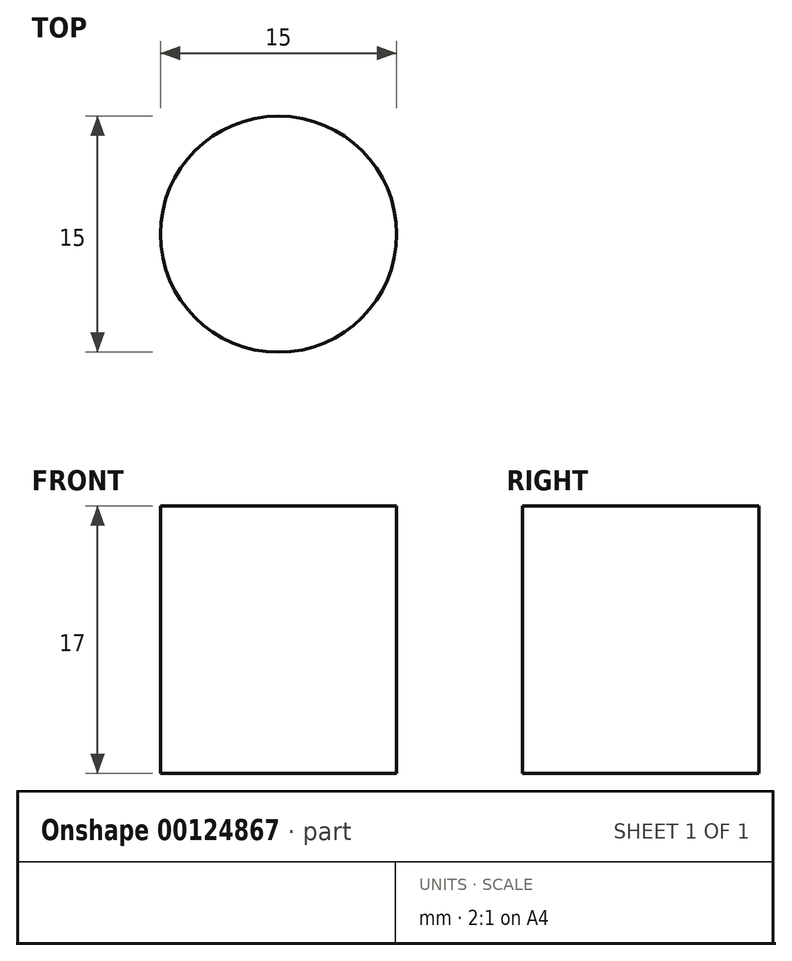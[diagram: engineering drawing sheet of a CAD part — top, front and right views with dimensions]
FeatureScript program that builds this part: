
annotation { "Feature Type Name" : "Feature", "Feature Type Description" : "" }
export const myFeature = defineFeature(function(context is Context, id is Id, definition is map)
    precondition{}
    {
        {
            var Q0;
            Q0=qCreatedBy(makeId("Top.planeOp"),FACE);
            var sketch = newSketch(context, id + "F0", { "sketchPlane" : qUnion([Q0])});
            skCircle(sketch, "E0", {"center": v(0, 0) * mm, "radius": 7.5 * mm});
            skSolve(sketch);
        }
        {
            var Q0;
            Q0 = qSketchRegion(id + "F0", true);
            extrude(context, id + "F1", {"entities" : qUnion([Q0]), "depth" : 17 * mm});
        }
    });
